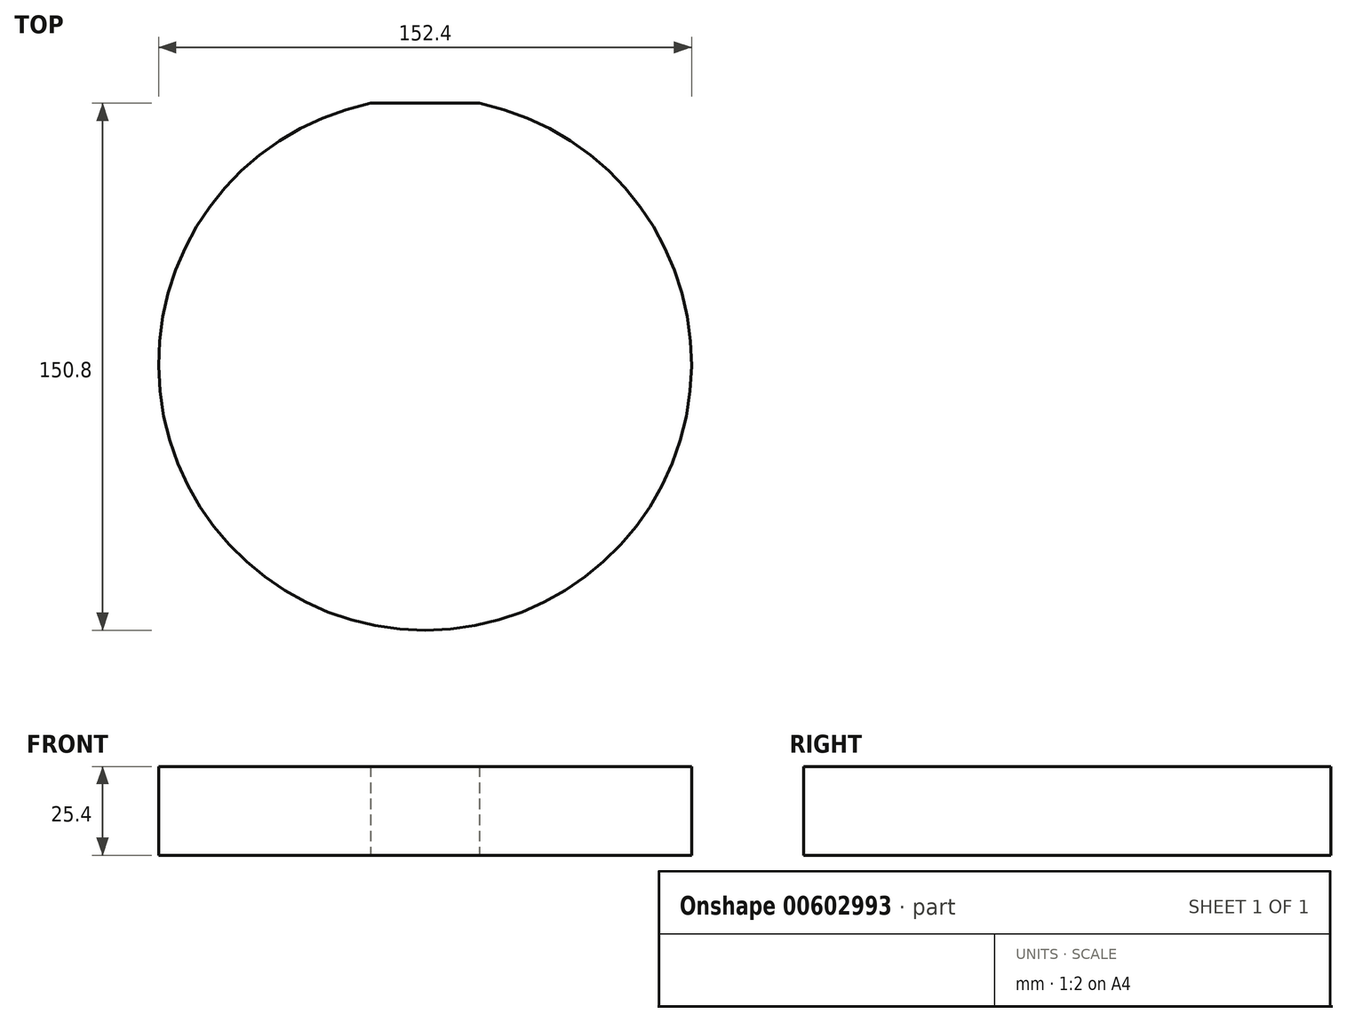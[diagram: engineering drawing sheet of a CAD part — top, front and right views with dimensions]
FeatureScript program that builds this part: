
annotation { "Feature Type Name" : "Feature", "Feature Type Description" : "" }
export const myFeature = defineFeature(function(context is Context, id is Id, definition is map)
    precondition{}
    {
        {
            var Q0;
            Q0=qCreatedBy(makeId("Top.planeOp"),FACE);
            var sketch = newSketch(context, id + "F0", { "sketchPlane" : qUnion([Q0])});
            skCircle(sketch, "E0", {"center": v(0, 0) * mm, "radius": 76.2 * mm});
            skLineSegment(sketch, "E1.bottom", {"start": v(-15.54, 74.6) * mm, "end": v(15.78, 74.6) * mm});
            skLineSegment(sketch, "E1.top", {"start": v(-15.54, -74.55) * mm, "end": v(15.78, -74.55) * mm});
            skLineSegment(sketch, "E1.left", {"start": v(-15.54, 74.6) * mm, "end": v(-15.54, -74.55) * mm});
            skLineSegment(sketch, "E1.right", {"start": v(15.78, 74.6) * mm, "end": v(15.78, -74.55) * mm});
            skSolve(sketch);
        }
        {
            var Q0;
            {var subQ2=sQuery(id+"F0.wireOp",EDGE,"E1.top");Q0=makeQuery(id+"F0.imprint","IMPRINT",FACE,{"disambiguationData":[TD([[makeQuery(id+"F0.imprint","IMPRINT",EDGE,{"derivedFrom":subQ2}),-1.0]])]});}
            var Q1;
            {var subQ1=sQuery(id+"F0.wireOp",EDGE,"E1.top");Q1=makeQuery(id+"F0.imprint","IMPRINT",FACE,{"disambiguationData":[TD([[makeQuery(id+"F0.imprint","IMPRINT",EDGE,{"derivedFrom":subQ1}),1.0]])]});}
            var Q2;
            {var subQ0=sQuery(id+"F0.wireOp",EDGE,"E1.right");var subQ1=sQuery(id+"F0.wireOp",EDGE,"E0");var subQ3=makeQuery(id+"F0.imprint","INTERSECT",VERTEX,{"derivedFrom":[subQ1,subQ0]});Q2=makeQuery(id+"F0.imprint","IMPRINT",FACE,{"disambiguationData":[TD([[makeQuery(id+"F0.imprint","IMPRINT",EDGE,{"disambiguationData":[TD([[subQ3,1.0]])],"derivedFrom":subQ1}),1.0]])]});}
            extrude(context, id + "F1", {"entities" : qUnion([Q0, Q1, Q2]), "depth" : 25.4 * mm, "offsetDistance" : 25.4 * mm});
        }
    });
